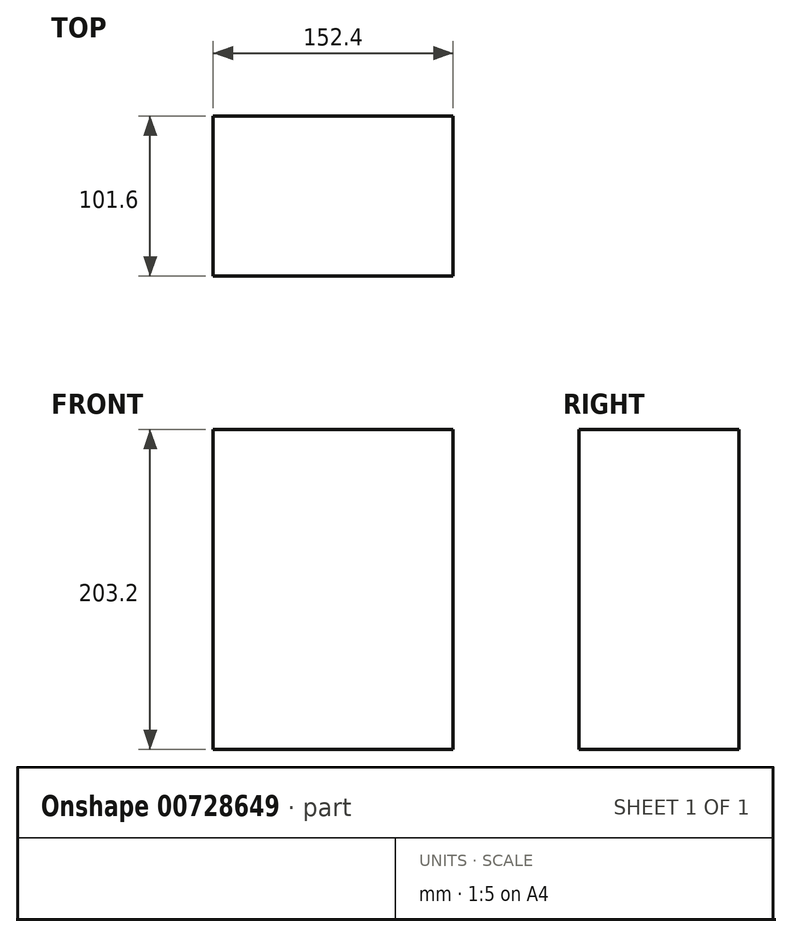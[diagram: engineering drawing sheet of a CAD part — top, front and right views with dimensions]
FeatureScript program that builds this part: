
annotation { "Feature Type Name" : "Feature", "Feature Type Description" : "" }
export const myFeature = defineFeature(function(context is Context, id is Id, definition is map)
    precondition{}
    {
        {
            var Q0;
            Q0=qCreatedBy(makeId("Front.planeOp"),FACE);
            var sketch = newSketch(context, id + "F0", { "sketchPlane" : qUnion([Q0])});
            skLineSegment(sketch, "E0.bottom", {"start": v(0, 0) * mm, "end": v(152.4, 0) * mm});
            skLineSegment(sketch, "E0.top", {"start": v(0, 203.2) * mm, "end": v(152.4, 203.2) * mm});
            skLineSegment(sketch, "E0.left", {"start": v(0, 0) * mm, "end": v(0, 203.2) * mm});
            skLineSegment(sketch, "E0.right", {"start": v(152.4, 0) * mm, "end": v(152.4, 203.2) * mm});
            skSolve(sketch);
        }
        {
            var Q0;
            Q0 = qSketchRegion(id + "F0", true);
            extrude(context, id + "F1", {"entities" : qUnion([Q0]), "depth" : 101.6 * mm, "offsetDistance" : 25.4 * mm});
        }
    });
